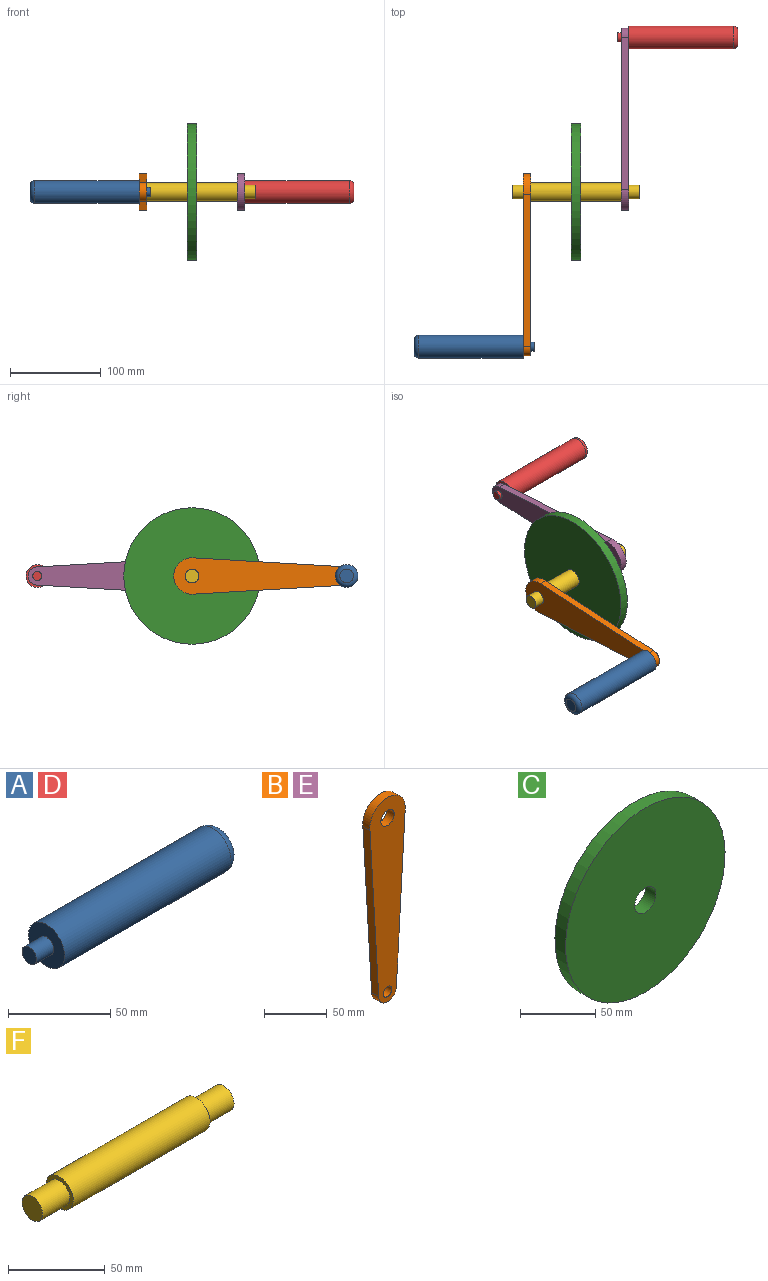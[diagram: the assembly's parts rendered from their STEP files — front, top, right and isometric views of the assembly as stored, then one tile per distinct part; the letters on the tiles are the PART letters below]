
ASSEMBLY  parts=6 mates=10
PART A: 6 faces, bbox 132x27.1x27.1 mm
  f0: plane 15x15mm, normal (1,0,0), area 176.7mm2, adj f1
  f1: torus R=7.5mm, axis (1,0,0), area 527.2mm2, adj f0,f2
  f2: cylinder r=12.5mm len=115mm, axis (1,0,0), area 9032.1mm2, adj f1,f3
  f3: plane 25x25mm, normal (-1,0,0), area 412.3mm2, adj f2,f4
  f4: cylinder r=5mm len=12mm, axis (1,0,0), area 377mm2, adj f3,f5
  f5: plane 10x10mm, normal (-1,0,0), area 78.5mm2, adj f4
PART B: 8 faces, bbox 40x8x200 mm
  f0: cylinder r=20mm len=40mm, axis (0,1,0), area 540.3mm2, adj f1,f3,f4,f5
  f1: plane 167.52x9.86mm, normal (-1,0,-0.06), area 1342.5mm2, adj f0,f2,f4,f5
  f2: cylinder r=10mm len=20mm, axis (0,1,0), area 255.1mm2, adj f1,f3,f4,f5
  f3: plane 167.3x9.87mm, normal (1,0,-0.06), area 1340.7mm2, adj f0,f2,f4,f5
  f4: plane 200x40mm, normal (0,-1,0), area 5627.3mm2, adj f0,f1,f2,f3,f6,f7
  f5: plane 200x40mm, normal (0,1,0), area 5627.3mm2, adj f0,f1,f2,f3,f6,f7
  f6: cylinder r=5mm len=10mm, axis (0,-1,0), area 251.3mm2, adj f4,f5
  f7: cylinder r=7.5mm len=15mm, axis (0,-1,0), area 377mm2, adj f4,f5
PART C: 4 faces, bbox 150x10x150 mm
  f0: cylinder r=10mm len=20mm, axis (0,1,0), area 628.3mm2, adj f2,f3
  f1: cylinder r=75mm len=150mm, axis (0,1,0), area 4712.4mm2, adj f2,f3
  f2: plane 150x150mm, normal (0,-1,0), area 17357.3mm2, adj f0,f1
  f3: plane 150x150mm, normal (0,1,0), area 17357.3mm2, adj f0,f1
PART D: same geometry as A
PART E: same geometry as B
PART F: 7 faces, bbox 140x20x20 mm
  f0: plane 15x15mm, normal (-1,0,0), area 176.7mm2, adj f6
  f1: plane 15x15mm, normal (1,0,0), area 176.7mm2, adj f2
  f2: cylinder r=7.5mm len=20mm, axis (1,0,0), area 942.5mm2, adj f1,f3
  f3: plane 20x20mm, normal (1,0,0), area 137.4mm2, adj f2,f4
  f4: cylinder r=10mm len=100mm, axis (1,0,0), area 6283.2mm2, adj f3,f5
  f5: plane 20x20mm, normal (-1,0,0), area 137.4mm2, adj f4,f6
  f6: cylinder r=7.5mm len=20mm, axis (1,0,0), area 942.5mm2, adj f0,f5
PLACE A rot(axis=(0,1,0),180deg) t=(-15.76,-200.15,-7.92)mm
PLACE B rot(axis=(-0.58,0.58,0.58),120deg) t=(-27.76,-30.15,-7.92)mm
PLACE C rot(axis=(0.58,0.58,-0.58),120deg) t=(35.24,-30.15,-7.92)mm
PLACE D t=(76.24,139.85,-7.92)mm
PLACE E rot(axis=(0.58,-0.58,0.58),120deg) t=(80.24,-30.15,-7.92)mm
PLACE F t=(-39.76,-30.15,-7.92)mm fixed
MATE planar F.f2 <-> B.f4  axis (-1,0,0) through (-19.76,-30.15,-7.92)mm
MATE planar C.f1 <-> F.f2  axis (1,0,0) through (35.24,-30.15,-7.92)mm
MATE planar D.f1 <-> E.f4  axis (-1,0,0) through (88.24,139.85,-7.92)mm
MATE planar E.f5 <-> F.f2  axis (-1,0,0) through (80.24,39.81,-7.92)mm
MATE slider B.f6 <-> A.f1  axis (1,0,0) through (-23.76,-200.15,-7.92)mm
MATE slider B.f7 <-> F.f2  axis (1,0,0) through (-23.76,-30.15,-7.92)mm
MATE planar A.f1 <-> B.f5  axis (1,0,0) through (-27.76,-200.15,-7.92)mm
MATE slider C.f0 <-> F.f2  axis (1,0,0) through (25.24,-30.15,-7.92)mm
MATE slider D.f1 <-> E.f6  axis (1,0,0) through (76.24,139.85,-7.92)mm
MATE slider E.f7 <-> F.f2  axis (1,0,0) through (88.24,-30.15,-7.92)mm
